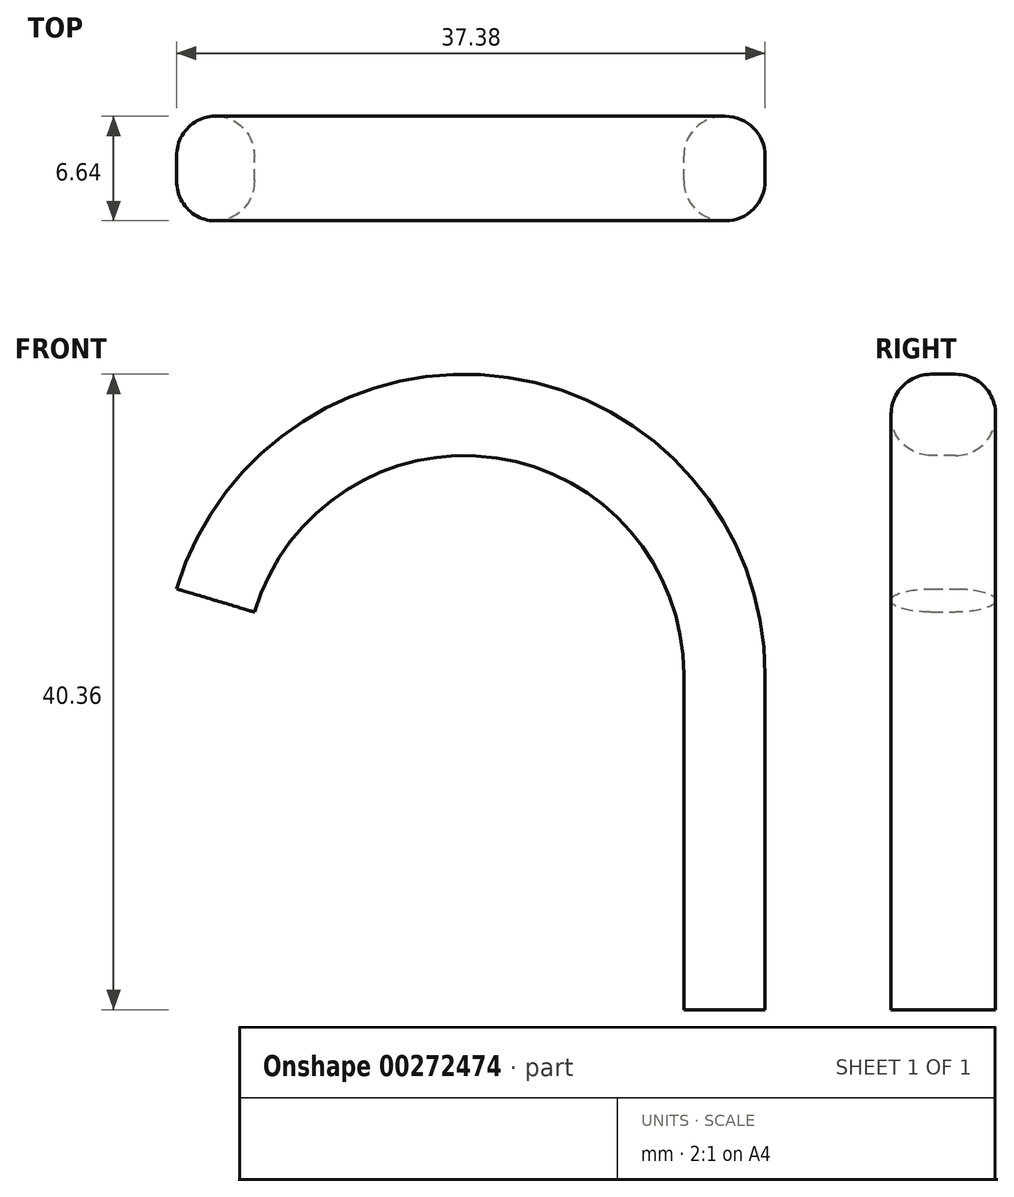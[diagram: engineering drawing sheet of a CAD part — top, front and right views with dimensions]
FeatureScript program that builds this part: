
annotation { "Feature Type Name" : "Feature", "Feature Type Description" : "" }
export const myFeature = defineFeature(function(context is Context, id is Id, definition is map)
    precondition{}
    {
        {
            var Q0;
            Q0=qCreatedBy(makeId("Top.planeOp"),FACE);
            var sketch = newSketch(context, id + "F0", { "sketchPlane" : qUnion([Q0])});
            skLineSegment(sketch, "E0.bottom", {"start": v(0.04, -3.32) * mm, "end": v(-0.04, -3.32) * mm});
            skLineSegment(sketch, "E0.top", {"start": v(0.04, 3.32) * mm, "end": v(-0.04, 3.32) * mm});
            skLineSegment(sketch, "E0.left", {"start": v(2.58, -0.78) * mm, "end": v(2.58, 0.78) * mm});
            skLineSegment(sketch, "E0.right", {"start": v(-2.58, -0.78) * mm, "end": v(-2.58, 0.78) * mm});
            skPoint(sketch, "E0.middle", {"position": v(0, 0) * mm});
            skPoint(sketch, "E1.visualSharp", {"position": v(2.58, 3.32) * mm});
            skArc(sketch, "E1.filletArc", {"start": v(2.58, 2.52) * mm, "mid": v(2.35, 3.09) * mm, "end": v(1.79, 3.32) * mm});
            skPoint(sketch, "E2.visualSharp", {"position": v(2.58, -3.32) * mm});
            skArc(sketch, "E2.filletArc", {"start": v(1.79, -3.32) * mm, "mid": v(2.35, -3.09) * mm, "end": v(2.58, -2.52) * mm});
            skPoint(sketch, "E3.visualSharp", {"position": v(-2.58, -3.32) * mm});
            skArc(sketch, "E3.filletArc", {"start": v(-2.58, -2.52) * mm, "mid": v(-2.35, -3.09) * mm, "end": v(-1.79, -3.32) * mm});
            skPoint(sketch, "E4.visualSharp", {"position": v(-2.58, 3.32) * mm});
            skArc(sketch, "E4.filletArc", {"start": v(-0.04, 3.32) * mm, "mid": v(-1.84, 2.57) * mm, "end": v(-2.58, 0.78) * mm});
            skArc(sketch, "E5.filletArc", {"start": v(2.58, 0.78) * mm, "mid": v(1.84, 2.57) * mm, "end": v(0.04, 3.32) * mm});
            skArc(sketch, "E6.filletArc", {"start": v(0.04, -3.32) * mm, "mid": v(1.84, -2.57) * mm, "end": v(2.58, -0.78) * mm});
            skArc(sketch, "E7.filletArc", {"start": v(-2.58, -0.78) * mm, "mid": v(-1.84, -2.57) * mm, "end": v(-0.04, -3.32) * mm});
            skSolve(sketch);
        }
        {
            var Q0;
            Q0=qCreatedBy(makeId("Front.planeOp"),FACE);
            var sketch = newSketch(context, id + "F1", { "sketchPlane" : qUnion([Q0])});
            skLineSegment(sketch, "E8", {"start": v(0, 0) * mm, "end": v(0, 21.27) * mm});
            skArc(sketch, "E9", {"start": v(0, 21.27) * mm, "mid": v(-14.12, 37.6) * mm, "end": v(-32.33, 26) * mm});
            skSolve(sketch);
        }
        {
            var Q0;
            Q0=makeQuery(id+"F0.imprint","IMPRINT",FACE,{"disambiguationData":[TD([[makeQuery(id+"F0.imprint","IMPRINT",EDGE,{"derivedFrom":sQuery(id+"F0.wireOp",EDGE,"E0.bottom")}),-1.0]])]});
            var Q1;
            Q1=sQuery(id+"F1.wireOp",EDGE,"E8");
            var Q2;
            Q2=sQuery(id+"F1.wireOp",EDGE,"E9");
            sweep(context, id + "F2", {"profiles" : qUnion([Q0]), "path" : qUnion([Q1, Q2])});
        }
    });
